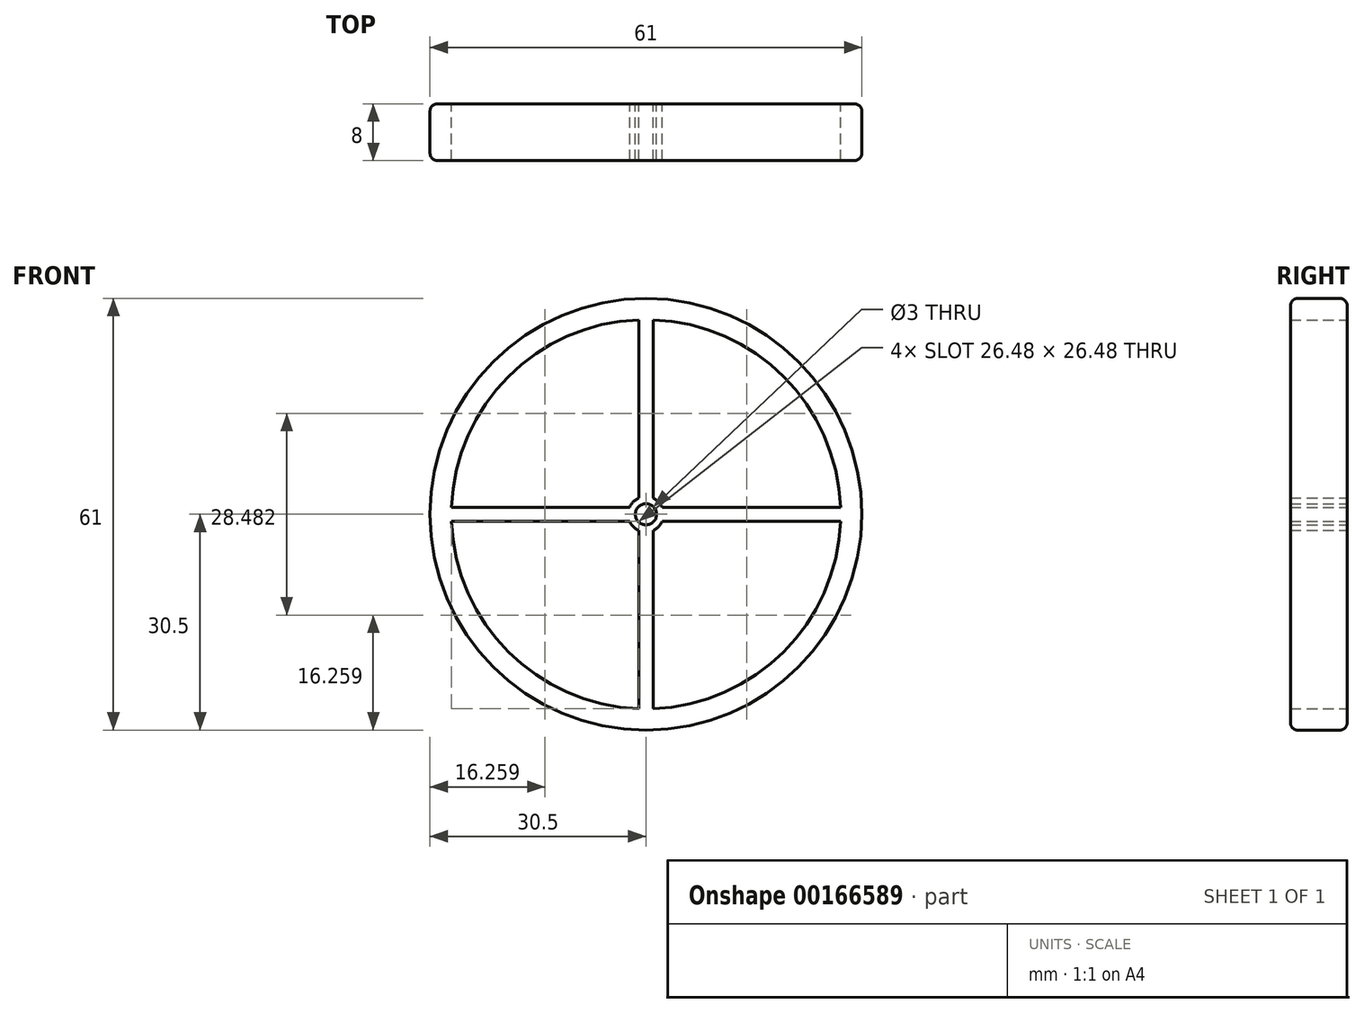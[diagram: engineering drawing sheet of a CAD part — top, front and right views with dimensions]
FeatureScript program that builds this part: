
annotation { "Feature Type Name" : "Feature", "Feature Type Description" : "" }
export const myFeature = defineFeature(function(context is Context, id is Id, definition is map)
    precondition{}
    {
        {
            var Q0;
            Q0=qCreatedBy(makeId("Front.planeOp"),FACE);
            var sketch = newSketch(context, id + "F0", { "sketchPlane" : qUnion([Q0])});
            skCircle(sketch, "E0", {"center": v(0, 0) * mm, "radius": 30.5 * mm});
            skArc(sketch, "E1.0", {"start": v(27.48, 1) * mm, "mid": v(19.45, 19.45) * mm, "end": v(1, 27.48) * mm});
            skArc(sketch, "E2.0", {"start": v(-2.3, -1) * mm, "mid": v(-1.77, -1.77) * mm, "end": v(-1, -2.3) * mm});
            skCircle(sketch, "E3.0", {"center": v(0, 0) * mm, "radius": 1.5 * mm});
            skLineSegment(sketch, "E4.bottom", {"start": v(2.3, 1) * mm, "end": v(27.48, 1) * mm});
            skLineSegment(sketch, "E4.top", {"start": v(2.3, -1) * mm, "end": v(27.48, -1) * mm});
            skLineSegment(sketch, "E5.MirrorCS", {"start": v(-2.3, -1) * mm, "end": v(-27.48, -1) * mm});
            skLineSegment(sketch, "E6.MirrorCS", {"start": v(-2.3, 1) * mm, "end": v(-27.48, 1) * mm});
            skPoint(sketch, "E7.MirrorCS.end.orphan", {"position": v(-2.3, -1) * mm});
            skPoint(sketch, "E7.MirrorCS.start.orphan", {"position": v(-2.3, 1) * mm});
            skArc(sketch, "E8.trimOffspring", {"start": v(2.3, 1) * mm, "mid": v(1.77, 1.77) * mm, "end": v(1, 2.3) * mm});
            skArc(sketch, "E9.trimOffspring", {"start": v(-27.48, -1) * mm, "mid": v(-19.45, -19.45) * mm, "end": v(-1, -27.48) * mm});
            skLineSegment(sketch, "E10.left", {"start": v(-1, 27.48) * mm, "end": v(-1, 2.3) * mm});
            skLineSegment(sketch, "E10.right", {"start": v(1, 27.48) * mm, "end": v(1, 2.3) * mm});
            skArc(sketch, "E11.trimOffspring", {"start": v(-1, 2.3) * mm, "mid": v(-1.77, 1.77) * mm, "end": v(-2.3, 1) * mm});
            skArc(sketch, "E12.trimOffspring", {"start": v(-1, 27.48) * mm, "mid": v(-19.45, 19.45) * mm, "end": v(-27.48, 1) * mm});
            skLineSegment(sketch, "E13.MirrorCS", {"start": v(-1, -27.48) * mm, "end": v(-1, -2.3) * mm});
            skLineSegment(sketch, "E14.MirrorCS", {"start": v(1, -27.48) * mm, "end": v(1, -2.3) * mm});
            skArc(sketch, "E15.trimOffspring", {"start": v(1, -27.48) * mm, "mid": v(19.45, -19.45) * mm, "end": v(27.48, -1) * mm});
            skArc(sketch, "E16.trimOffspring", {"start": v(1, -2.3) * mm, "mid": v(1.77, -1.77) * mm, "end": v(2.3, -1) * mm});
            skSolve(sketch);
        }
        {
            var Q0;
            Q0=makeQuery(id+"F0.imprint","IMPRINT",FACE,{"disambiguationData":[TD([[makeQuery(id+"F0.imprint","IMPRINT",EDGE,{"derivedFrom":sQuery(id+"F0.wireOp",EDGE,"E0")}),1.0]])]});
            extrude(context, id + "F1", {"entities" : qUnion([Q0]), "depth" : 8 * mm, "symmetric" : true});
        }
        {
            var Q0;
            Q0=makeQuery(id+"F1.opExtrude","CAP_EDGE",EDGE,{"disambiguationData":[OSD([sQuery(id+"F0.wireOp",EDGE,"E0")])],"isStart":false});
            var Q1;
            Q1=makeQuery(id+"F1.opExtrude","CAP_EDGE",EDGE,{"disambiguationData":[OSD([sQuery(id+"F0.wireOp",EDGE,"E0")])],"isStart":true});
            fillet(context, id + "F2", {"entities" : qUnion([Q0, Q1]), "radius" : 1 * mm, "tangentPropagation" : true, "allowEdgeOverflow" : false});
        }
    });
